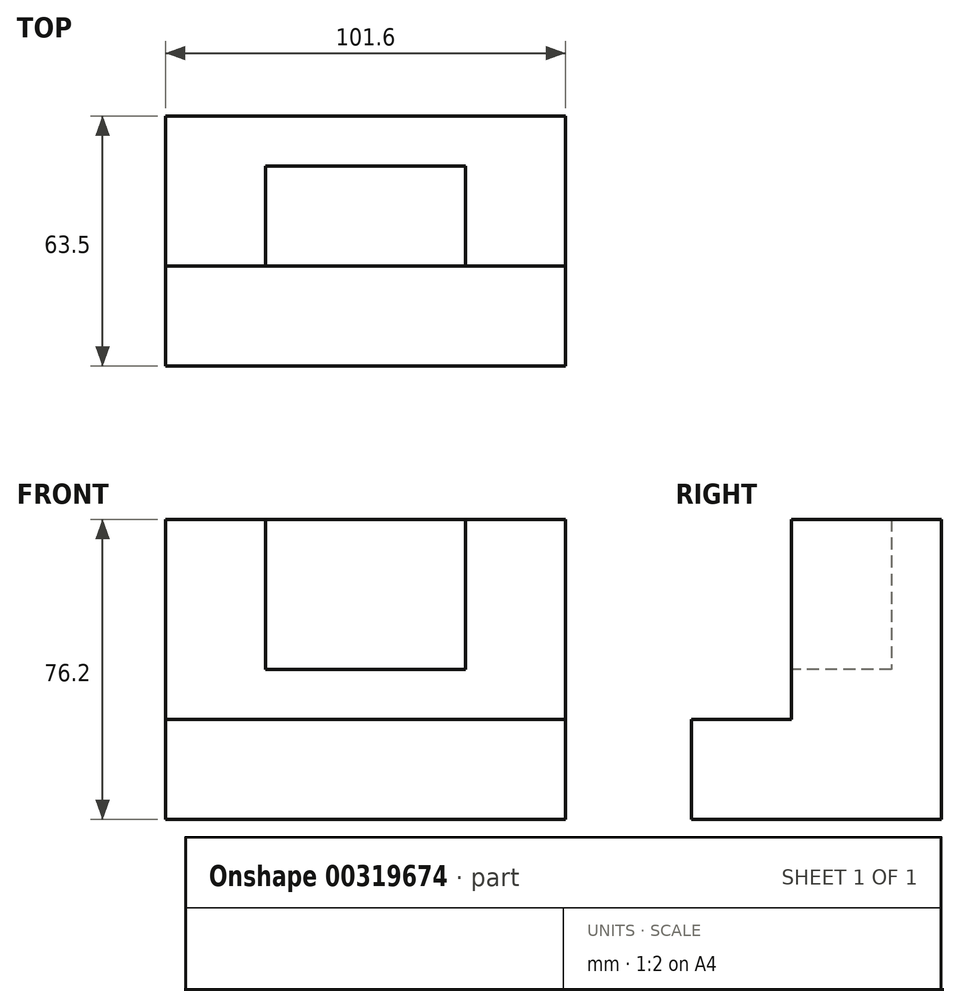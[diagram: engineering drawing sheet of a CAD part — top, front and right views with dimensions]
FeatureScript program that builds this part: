
annotation { "Feature Type Name" : "Feature", "Feature Type Description" : "" }
export const myFeature = defineFeature(function(context is Context, id is Id, definition is map)
    precondition{}
    {
        {
            var Q0;
            Q0=qCreatedBy(makeId("Right.planeOp"),FACE);
            var sketch = newSketch(context, id + "F0", { "sketchPlane" : qUnion([Q0])});
            skLineSegment(sketch, "E0", {"start": v(-34.24, -43.42) * mm, "end": v(29.26, -43.42) * mm});
            skLineSegment(sketch, "E1", {"start": v(29.26, -43.42) * mm, "end": v(29.26, 32.78) * mm});
            skLineSegment(sketch, "E2", {"start": v(29.26, 32.78) * mm, "end": v(-8.84, 32.78) * mm});
            skLineSegment(sketch, "E3", {"start": v(-8.84, 32.78) * mm, "end": v(-8.84, -18.02) * mm});
            skLineSegment(sketch, "E4", {"start": v(-8.84, -18.02) * mm, "end": v(-34.24, -18.02) * mm});
            skLineSegment(sketch, "E5", {"start": v(-34.24, -18.02) * mm, "end": v(-34.24, -43.42) * mm});
            skSolve(sketch);
        }
        {
            var Q0;
            Q0=makeQuery(id+"F0.imprint","IMPRINT",FACE,{"disambiguationData":[TD([[makeQuery(id+"F0.imprint","IMPRINT",EDGE,{"derivedFrom":sQuery(id+"F0.wireOp",EDGE,"E0")}),1.0]])]});
            extrude(context, id + "F1", {"entities" : qUnion([Q0]), "oppositeDirection" : true, "depth" : 101.6 * mm});
        }
        {
            var Q0;
            Q0=makeQuery(id+"F1.opExtrude","SWEPT_FACE",FACE,{"disambiguationData":[OSD([sQuery(id+"F0.wireOp",EDGE,"E3")])]});
            var sketch = newSketch(context, id + "F2", { "sketchPlane" : qUnion([Q0])});
            skLineSegment(sketch, "E6", {"start": v(-25.4, 32.78) * mm, "end": v(-25.4, -5.32) * mm});
            skLineSegment(sketch, "E7", {"start": v(-25.4, -5.32) * mm, "end": v(-76.2, -5.32) * mm});
            skLineSegment(sketch, "E8", {"start": v(-76.2, -5.32) * mm, "end": v(-76.2, 32.78) * mm});
            skSolve(sketch);
        }
        {
            var Q0;
            Q0 = qSketchRegion(id + "F2", true);
            var Q1;
            {var subQ0=sQuery(id+"F2.wireOp",EDGE,"E6");Q1=makeQuery(id+"F2.imprint","IMPRINT",FACE,{"disambiguationData":[TD([[makeQuery(id+"F2.imprint","IMPRINT",EDGE,{"derivedFrom":subQ0}),-1.0]])]});}
            extrude(context, id + "F3", {"entities" : qUnion([Q0, Q1]), "operationType" : NewBodyOperationType.REMOVE, "oppositeDirection" : true, "depth" : 25.4 * mm});
        }
    });
